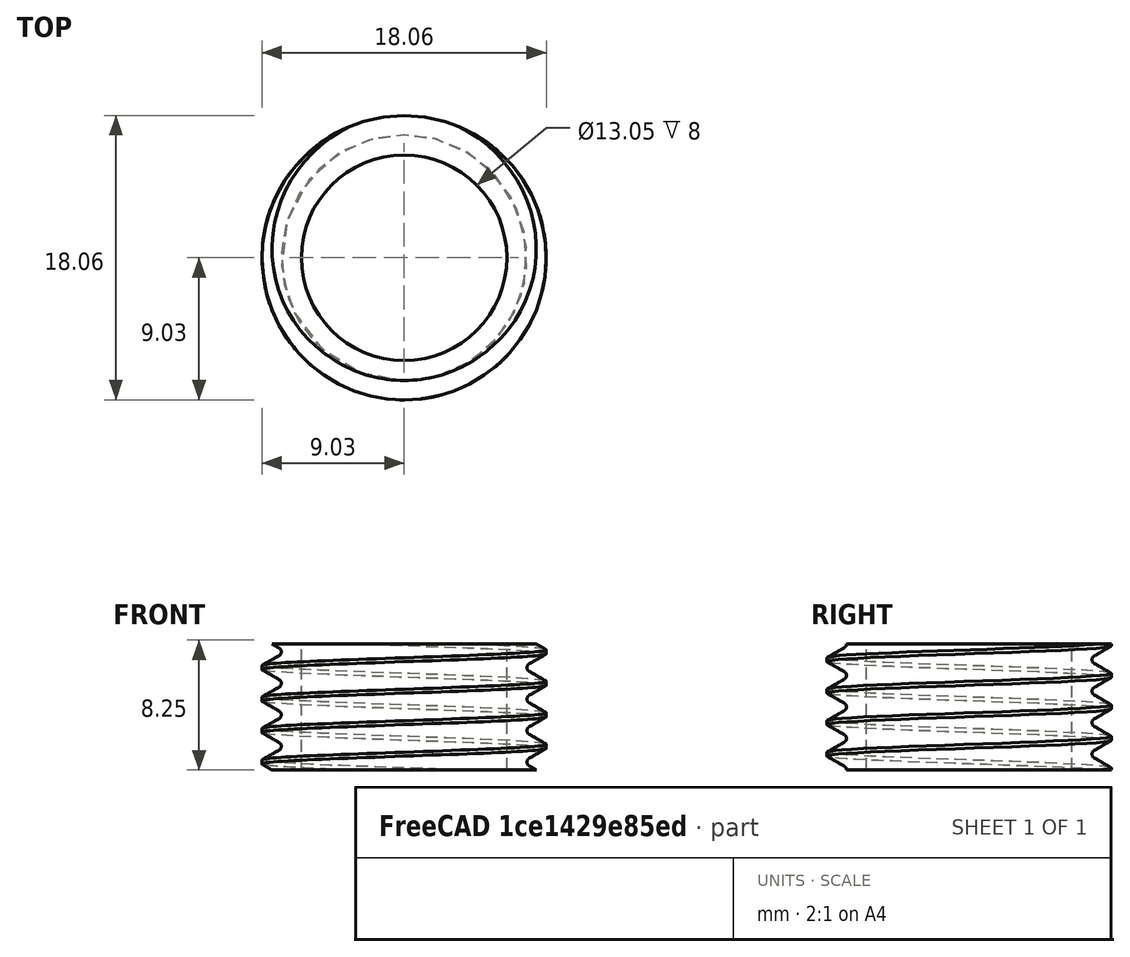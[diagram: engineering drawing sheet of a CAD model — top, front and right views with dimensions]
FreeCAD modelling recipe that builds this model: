
FCSTD DOCUMENT  (FreeCAD 0.18R16110 (Git))
Label: P1000_Bolt
License: All rights reserved
LicenseURL: http://en.wikipedia.org/wiki/All_rights_reserved
objects: Part::Cylinder×2, Part::Cut×2, Part::Helix×1, Sketcher::SketchObject×1, Part::Sweep×1, Spreadsheet::Sheet×1, Mesh::Feature×1
note: 7 computed .brp shape members not serialized (recipe doc carries the construction recipe); baked Part::Feature solids carry a one-line shape summary decoded from their .brp

FEATURE [Part::Helix] Helix
  Angle = 0
  AttacherType = Attacher::AttachEngine3D
  Height = 13
  LocalCoord = 0
  Pitch = 2
  Placement = pos=(0,0,-2) rot=(0,0,1;0rad)
  Radius = 9.025
  Style = 1
  expr: Radius = Spreadsheet.B11
  expr: Height = Spreadsheet.B3 + 5
  expr: Pitch = Spreadsheet.B1
FEATURE [Part::Cylinder] Cylinder  label="Zylinder"
  Angle = 360
  AttacherType = Attacher::AttachEngine3D
  Height = 8
  Radius = 9.025
  expr: Height = Spreadsheet.B3
  expr: Radius = Spreadsheet.B11
FEATURE [Sketcher::SketchObject] Sketch
  AttachmentOffset = pos=(0,1,0) rot=(0,0,1;0rad)
  MapMode = 3
  Placement = pos=(0,2e-16,1) rot=(1,0,0;1.5708rad)
  Support = -> [Cylinder]
  expr: Constraints[27] = Spreadsheet.B1 / 4 / 2
  expr: Constraints[22] = Spreadsheet.B2 / 8
  expr: Constraints[26] = Spreadsheet.B2 * 6 / 8
  expr: Constraints[2] = Spreadsheet.B11
  expr: Constraints[23] = Spreadsheet.B1 / 2
  sketch-geometry (10):
    g0: LineSegment [constr] StartX=0 StartY=0 StartZ=0 EndX=9.025 EndY=0 EndZ=0
    g1: LineSegment [constr] StartX=9.025 StartY=0 StartZ=0 EndX=9.24151 EndY=0 EndZ=0
    g2: LineSegment [constr] StartX=9.24151 StartY=1 StartZ=0 EndX=7.94247 EndY=1 EndZ=0
    g3: LineSegment StartX=9.24151 StartY=0 StartZ=0 EndX=9.24151 EndY=1 EndZ=0
    g4: LineSegment StartX=9.24151 StartY=1 StartZ=0 EndX=9.24151 EndY=2 EndZ=0
    g5: LineSegment [constr] StartX=7.94247 StartY=1 StartZ=0 EndX=7.94247 EndY=1.25 EndZ=0
    g6: LineSegment [constr] StartX=7.94247 StartY=1 StartZ=0 EndX=7.94247 EndY=0.75 EndZ=0
    g7: LineSegment StartX=7.94247 StartY=1.25 StartZ=0 EndX=9.24151 EndY=2 EndZ=0
    g8: LineSegment StartX=7.94247 StartY=0.75 StartZ=0 EndX=9.24151 EndY=0 EndZ=0
    g9: ArcOfCircle CenterX=8.0868 CenterY=1 CenterZ=0 NormalX=0 NormalY=0 NormalZ=1 AngleXU=0 Radius=0.288673 StartAngle=2.09438 EndAngle=4.1888
  constraints (28):
    c: Coincident(g0,g-1)
    c: Horizontal(g0)
    c: DistanceX(g0,g0) = 9.025
    c: Coincident(g1,g0)
    c: Horizontal(g1)
    c: Horizontal(g2)
    c: Coincident(g3,g2)
    c: Vertical(g3)
    c: Coincident(g4,g2)
    c: Vertical(g4)
    c: Equal(g4,g3)
    c: Coincident(g5,g2)
    c: Vertical(g5)
    c: Coincident(g6,g2)
    c: Vertical(g6)
    c: Equal(g5,g6)
    c: Coincident(g7,g4)
    c: Coincident(g8,g6)
    c: Coincident(g9,g7)
    c: Coincident(g9,g6)
    c: Coincident(g7,g5)
    c: Tangent(g9,g8)
    c: DistanceX(g1,g1) = 0.216506
    c: DistanceY(g3,g3) = 1
    c: Coincident(g3,g1)
    c: Coincident(g8,g1)
    c: DistanceX(g2,g2) = 1.29904
    c: DistanceY(g6,g6) = 0.25
FEATURE [Part::Sweep] Sweep
  Frenet = true
  Sections = -> [Sketch]
  Solid = true
  Spine = -> Helix [Edge1,Edge2,Edge3,Edge4,Edge5,Edge6,Edge7]
  Transition = 1
FEATURE [Part::Cylinder] Cylinder001  label="Zylinder001"
  Angle = 360
  AttacherType = Attacher::AttachEngine3D
  Height = 8
  Radius = 6.525
  expr: Radius = Spreadsheet.B13
  expr: Height = Spreadsheet.B3
FEATURE [Part::Cut] Cut
  Base = -> Cylinder
  Tool = -> Cylinder001
FEATURE [Part::Cut] Cut001  label="P1000_Bolt"
  Base = -> Cut
  Placement = pos=(0,0,-58) rot=(0,0,-1;1.5708rad)
  Tool = -> Sweep
FEATURE [Spreadsheet::Sheet] Spreadsheet
  cells = A1=Steigung; B1=2; A2=H; B2==sqrt((B1 / 2 / sin(60 / 2)) ^ 2 - (B1 / 2) ^ 2); A3=h; B3=8; A5=Nut; A6=ra; B6=11; A7=si; B7=2; A8=ri; B8==B11 - 5 / 8 * B2 + B15; A10=Bolt; A11=ra; B11==18.45 / 2 - B15; A12=si; B12=2.5; A13=ri; B13==B11 - B12; A15=tolerance; B15=0.2
FEATURE [Mesh::Feature] Mesh  label="P1000_Bolt (Meshed)"
